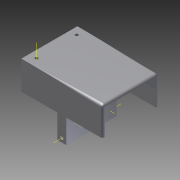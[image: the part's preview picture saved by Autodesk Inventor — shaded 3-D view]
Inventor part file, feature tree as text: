
AUTODESK INVENTOR PART (.ipt)
format: ipt  version: 2012 (Build 160160000, 160)  size: 291,328 bytes
history: native  units: mm
features: extrude x13, sketch x13, reference x9, projected_geometry x9, plane x4, fillet x3, other x3
ambient origin geometry x8: Origin, YZ Plane, XZ Plane, XY Plane, X Axis, Y Axis, Z Axis, Center Point
bodies: Solid1 (feature_tree)
feature tree (54):
  extrude  "Extrusion1"  Depth=2.0mm TaperAngle=0.0deg
  extrude  "Extrusion2"  TaperAngle=45.0deg  [1 undecoded]
  extrude  "Extrusion3"  Depth=9.0mm
  sketch  "Sketch4"  dims[d8=2.0mm d9=0.0mm d10=8.0mm]
  plane  "Work Plane1"
  plane  "Work Plane2"
  extrude  "Extrusion4"  Depth=8.0mm
  extrude  "Extrusion5"  Depth=0.3mm TaperAngle=0.0deg
  extrude  "Extrusion6"  Depth=0.3mm
  extrude  "Extrusion7"  Depth=0.3mm
  extrude  "Extrusion8"  Depth=0.3mm TaperAngle=0.0deg
  extrude  "Extrusion9"  Depth=7.4mm
  extrude  "Extrusion10"  Depth=3.25mm
  plane  "Work Plane3"
  extrude  "Extrusion12"  Depth=5.0mm TaperAngle=0.0deg
  extrude  "Extrusion13"  Depth=0.3mm TaperAngle=0.0deg
  sketch  "Sketch18"  dims[d45=0.3mm d46=0.0mm d47=0.3mm d48=0.0mm d55=2.0mm d56=0.0mm d57=0.0mm d58=2.0mm d59=2.0mm]
  plane  "Work Plane4"
  extrude  "Extrusion14"  Depth=0.3mm TaperAngle=0.0deg
  fillet  "Fillet6"  Radius=2.0mm
  fillet  "Fillet7"  [1 undecoded]
  other  "Work Axis1"
  other  "Work Axis2"
  fillet  "Fillet8"  [1 undecoded]
  other  "Work Axis3"
  sketch  "Sketch1"  dims[d0=24.0mm d1=0.0mm d2=2.0mm d3=0.0mm]
  reference  "Reference1"
  reference  "Reference2"
  sketch  "Sketch2"  dims[d4=45.0deg d5=45.0deg]
  projected_geometry  "Projected Loop1"
  projected_geometry  "Projected Loop2"
  sketch  "Sketch3"  dims[d6=9.0mm d7=9.0mm]
  projected_geometry  "Projected Loop3"
  reference  "Reference3"
  reference  "Reference4"
  sketch  "Sketch6"  dims[d11=2.0mm d12=0.0mm d13=0.3mm d14=0.0mm]
  sketch  "Sketch7"  dims[d16=0.5mm d17=0.0mm d19=0.3mm]
  reference  "Reference8"
  sketch  "Sketch8"  dims[d21=0.3mm d22=0.3mm]
  sketch  "Sketch9"  dims[d23=0.5mm d24=0.0mm d25=0.3mm d26=0.0mm]
  projected_geometry  "Projected Loop4"
  sketch  "Sketch11"  dims[d27=0.3mm d28=7.4mm]
  projected_geometry  "Projected Loop5"
  sketch  "Sketch12"  dims[d29=3.7mm d30=3.25mm]
  sketch  "Sketch15"  dims[d31=2.5mm d32=5.0mm d33=0.0mm]
  projected_geometry  "Projected Loop9"
  sketch  "Sketch16"  dims[d34=5.0mm d35=0.0mm d43=0.3mm d44=0.0mm]
  reference  "Reference9"
  reference  "Reference10"
  projected_geometry  "Projected Loop10"
  projected_geometry  "Projected Loop11"
  projected_geometry  "Projected Loop12"
  reference  "Reference13"
  reference  "Reference14"
note: 3 required parameter values undecoded (feature->parameter linkage not recoverable at this tier; creation-order binding heuristic only, values carry confidence <= 0.55)
